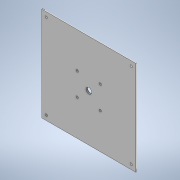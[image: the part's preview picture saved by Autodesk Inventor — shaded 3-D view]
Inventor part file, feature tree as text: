
AUTODESK INVENTOR PART (.ipt)
format: ipt  version: 2022 (Build 260153000, 153)  size: 191,488 bytes
history: native  units: in
note: dims shown in document units (in); Inventor stores cm internally (conversion verified against a paired STEP export)
features: sketch x4, extrude x3, fillet x1
ambient origin geometry x8: Origin, YZ Plane, XZ Plane, XY Plane, X Axis, Y Axis, Z Axis, Center Point
bodies: Solid1 (feature_tree)
feature tree (8):
  extrude  "Extrusion1"  Depth=5.0in
  extrude  "Extrusion2"  Depth=0.12in
  fillet  "Fillet1"  Radius=0.12in
  extrude  "Extrusion3"  Depth=0.25in
  sketch  "Sketch5"  dims[d7=0.25in d8=0.25in d9=0.125in d10=0.0in d11=0.3in d12=0.12in d13=0.12in d14=0.12in d15=0.12in d16=1.22in d19=1.0in d20=0.0in d21=1.22in d22=1.22in d23=0.125in d24=2.0in d25=0.5in d26=0.2953in d27=0.2953in d28=0.0738in d29=0.0738in d30=0.0394in d31=0.0in]
  sketch  "Sketch1"  dims[d0=5.0in d1=5.0in]
  sketch  "Sketch2"  dims[d2=5.0in d3=0.12in d4=0.12in]
  sketch  "Sketch4"  dims[d5=0.25in d6=0.25in]
